# Revit family: DHB-E LCD (mm)
name_source: partatom
category: Electrical Equipment
revit_build: Autodesk Revit 2018 (Build: 20180329_1100(x64)
units: mm (PartAtom-declared; Revit-internal decimal feet)

## family parameters
Always vertical = No
Cut with Voids When Loaded = No
OmniClass Number = 23.31.29.11.11
OmniClass Title = Electric Instantaneous Hot Water Heaters
Part Type = Other Panel
Room Calculation Point = No
Round Connector Dimension = Use Diameter
Shared = No
Work Plane-Based = Yes

## types (4) — shared parameters
Color = White
Construction = pressure
Default Elevation = 1219 mm
Depth = 116 mm
Edition number = 1
Electrical connection = 3/P
Energy efficiency class = A
Heating system = Bare wire
Height = 466 mm
IP rating = IP 25
Manufacturer = Stiebel Eltron Gesellschaft m.b.H.
Manufacturer name = Stiebel Eltron GmbH
Material Black Plastic = Stiebel Eltron - Plastic - Black
Material Cover = Stiebel Eltron - Plastic - White
Material Transparent Plastic = Stiebel Eltron - Plastic - Transparent Grey
Nominal overpressure = 1 MPa (10)
Pipe outside diameter cold drinking water = 22 mm
Pipe outside diameter of warm drinking water = 22 mm
Product Guid = c928bee9-0f29-4ce3-82ac-4540df086e6a
Product SKU = dhb-e_lcd
Product data url = https://bimobject.com
Product name = DHB-E LCD
QR code = https://bimobject.com
Switch-on quantity = 2,5
Temperature selection = Off, 20–60 °C
Type of scheme = electronic
URL = https://www.stiebel-eltron.de
Water connection = G 1/2
Width = 225 mm
nominal capacity = 0.4l

## per-type parameters (varying)
| type | Frequency | Fuse protection | Model | Rated current | Rated output | Weight |
| Type - (DHB-E LCD 236745) Power - (18/21/24 kW) | 50/60 Hz | 32/32/35 A | DHB-E 18/21/24 LCD | 29/31/35 A | 18/21/24 kW | 2,90 kg |
| Type - (DHB-E LCD 236746) Power - (27 kW) | 50/- Hz | 40 A | DHB-E 27 LCD | 39 A | 27 kW | 2.90 kg |
| Type - (DHB-E LCD 236743) Power -  (11/13.5 kW) | 50/60 Hz | 20 A | DHB-E 11/13 LCD | 17.5/19.5 A | 11/13.5 kW | 2.80 kg |
| Type - (DHB-E LCD 236744) Power -  (18 kW) | 50/60 Hz | 25 A | DHB-E 18 LCD 25A | 26 A | 18 kW | 2.90 kg |

## geometry (parser evidence)
native form markers: Sweep x2
no freeform markers — native parametric forms only
